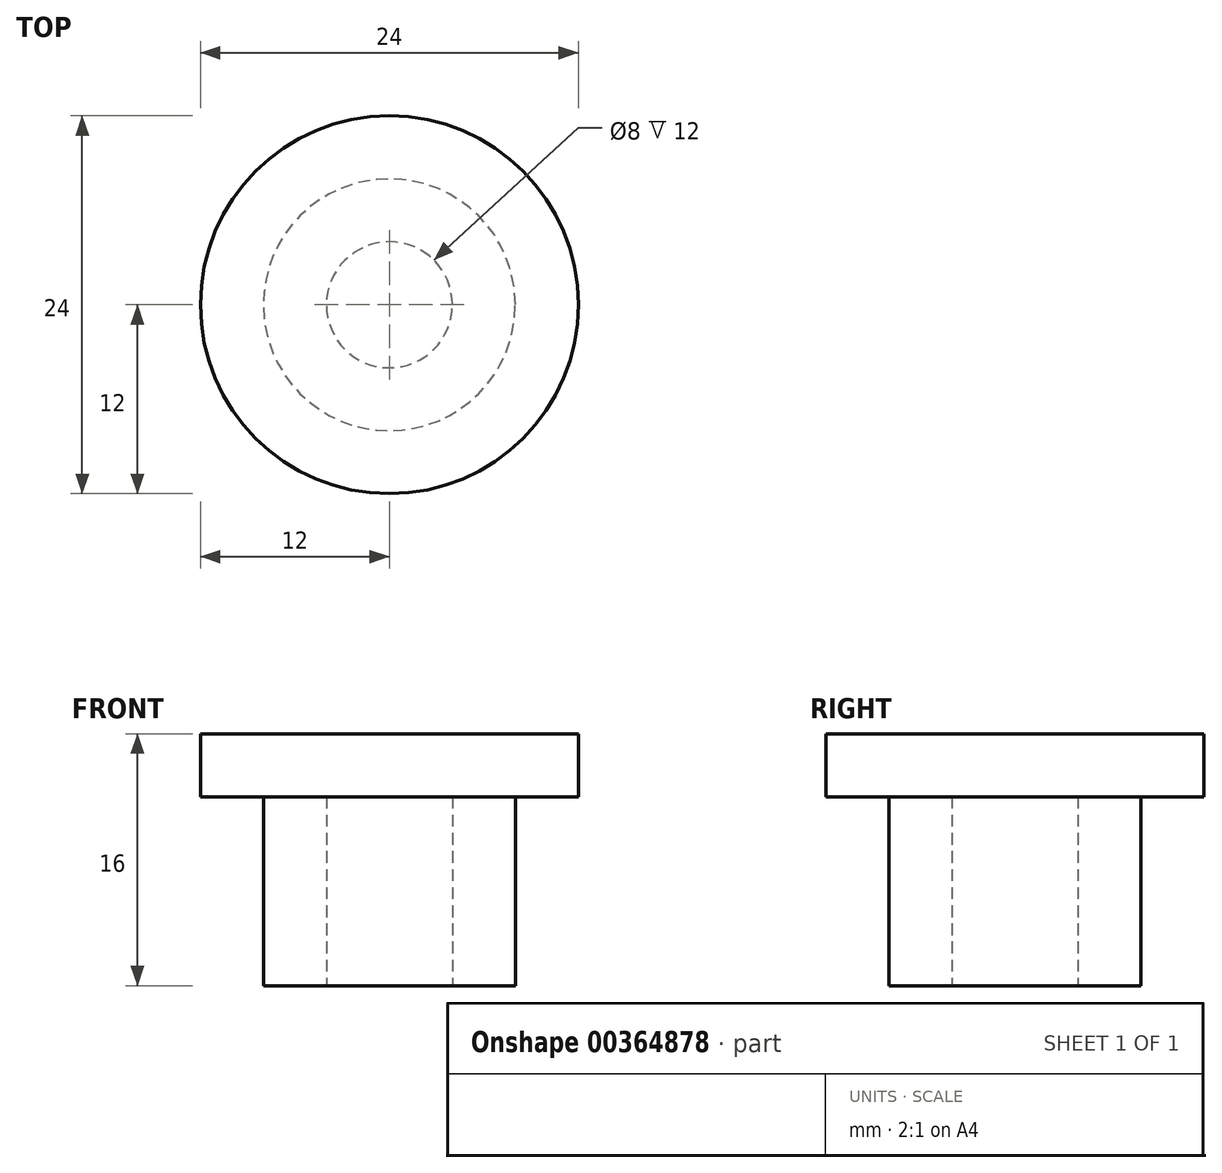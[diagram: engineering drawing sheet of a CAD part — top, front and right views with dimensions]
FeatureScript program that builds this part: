
annotation { "Feature Type Name" : "Feature", "Feature Type Description" : "" }
export const myFeature = defineFeature(function(context is Context, id is Id, definition is map)
    precondition{}
    {
        {
            var Q0;
            Q0=qCreatedBy(makeId("Top.planeOp"),FACE);
            var sketch = newSketch(context, id + "F0", { "sketchPlane" : qUnion([Q0])});
            skCircle(sketch, "E0", {"center": v(0, 0) * mm, "radius": 4 * mm});
            skCircle(sketch, "E1", {"center": v(0, 0) * mm, "radius": 8 * mm});
            skSolve(sketch);
        }
        {
            var Q0;
            Q0 = qSketchRegion(id + "F0", true);
            extrude(context, id + "F1", {"entities" : qUnion([Q0]), "depth" : 12 * mm});
        }
        {
            var Q0;
            Q0=makeQuery(id+"F1.opExtrude","CAP_FACE",FACE,{"disambiguationData":[OSD([sQuery(id+"F0.wireOp",EDGE,"E0"),sQuery(id+"F0.wireOp",EDGE,"E1")])],"isStart":false});
            cPlane(context, id + "F2", {"entities" : qUnion([Q0]), "cplaneType" : CPlaneType.OFFSET, "offset" : 0 * mm, "width" : 150 * mm, "height" : 150 * mm});
        }
        {
            var Q0;
            Q0=qCreatedBy(id+"F2.planeOp",FACE);
            var sketch = newSketch(context, id + "F3", { "sketchPlane" : qUnion([Q0])});
            skCircle(sketch, "E2", {"center": v(0, 0) * mm, "radius": 12 * mm});
            skSolve(sketch);
        }
        {
            var Q0;
            Q0 = qSketchRegion(id + "F3", true);
            extrude(context, id + "F4", {"entities" : qUnion([Q0]), "operationType" : NewBodyOperationType.ADD, "depth" : 4 * mm});
        }
    });
